# Revit family: G-Sill -S405
name_source: partatom
category: Generic Models
units: mm (PartAtom-declared; Revit-internal decimal feet)

## family parameters
Always vertical = Yes
Can host rebar = No
Cut with Voids When Loaded = No
Part Type = Normal
Room Calculation Point = No
Round Connector Dimension = Use Diameter
Shared = No
Work Plane-Based = No

## types (1)
- G-Sill -S405
    Construction Type = Precast
    Default Elevation = 0 mm  [stored 0 ft]
    Description = Type G-Sill
    Detailing = As per design specification and product drawings.
    Distance from Face to Seating = 170 mm  [stored 0.557743 ft]
    Front Face Dimension = 60 mm  [stored 0.19685 ft]
    Keynote = The information contained is the sole property of KPC Ltd., any reproduction in part or whole without permission of KPC Ltd. is prohibited.
    Length Options = All sizes made to order.
    Load Bearing = No
    Manufacturer = Killeshal Precast Concrete Ltd.
    Model = S/405 Sill
    Service Life = 0.000000
    Shape = As per drawing
    Size = 210mm x 115 to 60mm
    Slope = 0.00°
    Span = Ope Size + 205mm overhang.
    Type Comments = Visit our website for a full list of available products.
    Types = Single
    URL = www.killeshal.com
    Weight = 40Kg/m
    Width of Seating = 31 mm  [stored 0.101706 ft]

note: [stored X ft] marks values corroborated as IEEE doubles in the binary element streams (Revit-internal decimal feet)

## geometry (parser evidence)
native form markers: Sweep x3
no freeform markers — native parametric forms only
